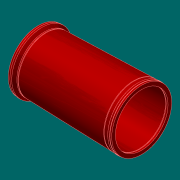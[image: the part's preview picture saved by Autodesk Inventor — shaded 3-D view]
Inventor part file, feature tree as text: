
AUTODESK INVENTOR PART (.ipt)
format: ipt  version: 2017.3 (Build 213256000, 256)  size: 181,760 bytes
history: native  units: in
note: dims shown in document units (in); Inventor stores cm internally (conversion verified against a paired STEP export)
features: revolve x1, fillet x1, sketch x1
ambient origin geometry x8: Origin, YZ Plane, XZ Plane, XY Plane, X Axis, Y Axis, Z Axis, Center Point
bodies: Solid1 (feature_tree)
feature tree (3):
  revolve  "Revolution1"  [1 undecoded]
  fillet  "Fillet1"  Radius=28.5in
  sketch  "Sketch1"  dims[d0=55.9843in d1=26.0in d2=28.5in d3=32.48in d4=2.0in d5=1.0in d6=1.0in d7=32.48in d8=30.0in d9=1.0in d10=4.0in d11=12.0in d12=12.0in d13=48.0in d14=2.0779in d15=90.0deg d16=0.0312in d17=1.0in d18=45.0deg d19=32.75in d23=1.0in d24=45.0deg d25=32.75in]
note: 1 required parameter value undecoded (feature->parameter linkage not recoverable at this tier; creation-order binding heuristic only, values carry confidence <= 0.55)
